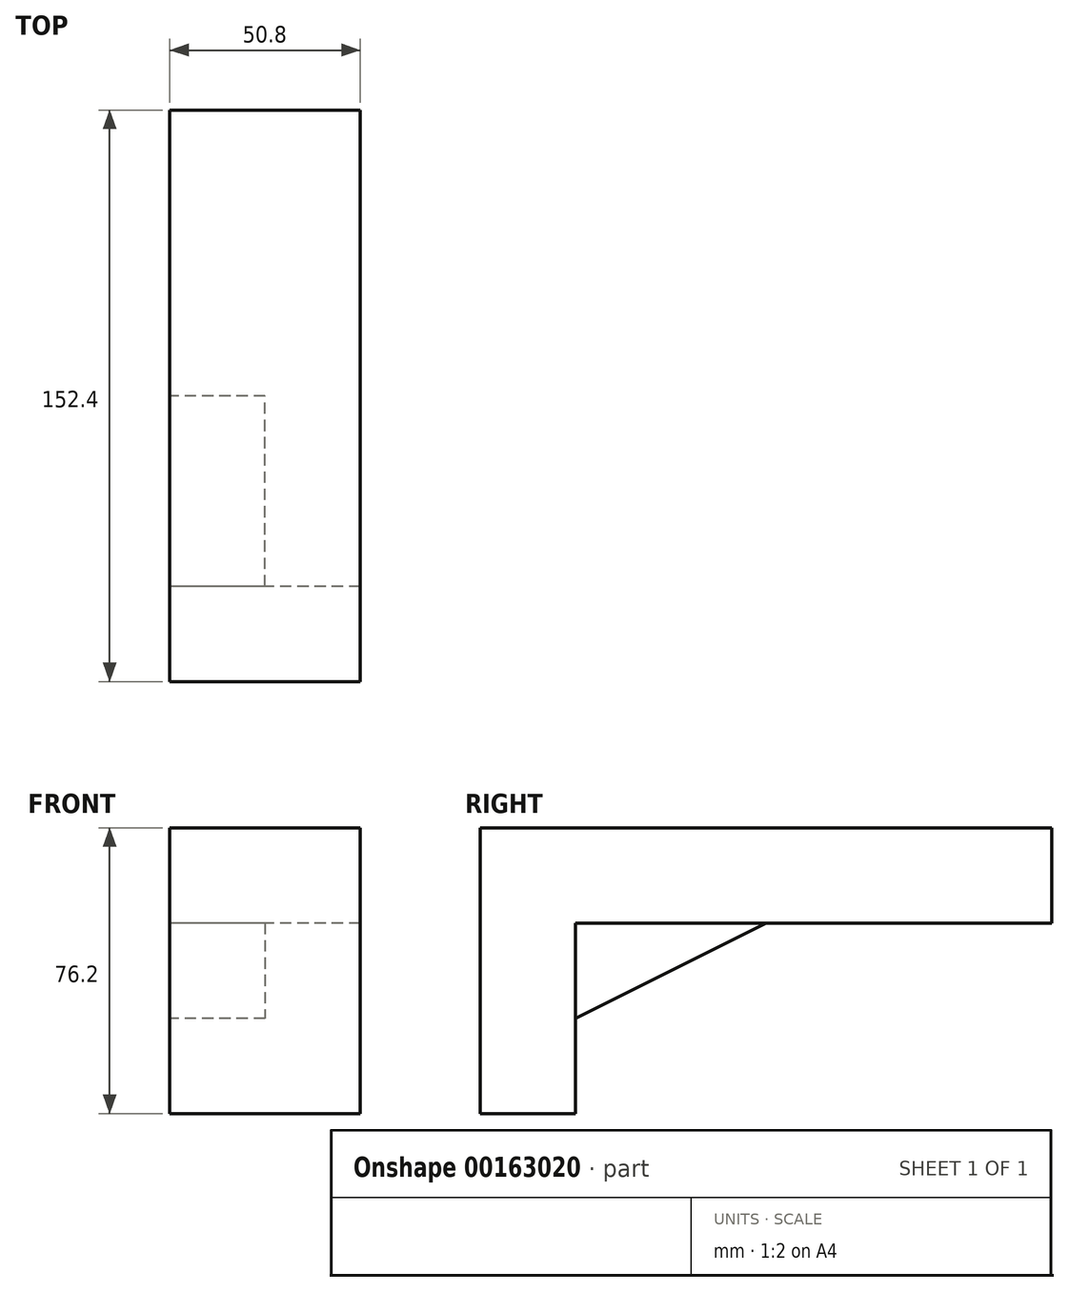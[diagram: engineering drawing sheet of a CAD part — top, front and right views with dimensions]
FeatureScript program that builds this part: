
annotation { "Feature Type Name" : "Feature", "Feature Type Description" : "" }
export const myFeature = defineFeature(function(context is Context, id is Id, definition is map)
    precondition{}
    {
        {
            var Q0;
            Q0=qCreatedBy(makeId("Right.planeOp"),FACE);
            var sketch = newSketch(context, id + "F0", { "sketchPlane" : qUnion([Q0])});
            skLineSegment(sketch, "E0", {"start": v(0, 0) * mm, "end": v(0, 76.2) * mm});
            skLineSegment(sketch, "E1", {"start": v(0, 0) * mm, "end": v(25.4, 0) * mm});
            skLineSegment(sketch, "E2", {"start": v(0, 76.2) * mm, "end": v(152.4, 76.2) * mm});
            skLineSegment(sketch, "E3", {"start": v(25.4, 0) * mm, "end": v(25.4, 50.8) * mm});
            skLineSegment(sketch, "E4", {"start": v(152.4, 76.2) * mm, "end": v(152.4, 50.8) * mm});
            skLineSegment(sketch, "E5", {"start": v(25.4, 50.8) * mm, "end": v(152.4, 50.8) * mm});
            skSolve(sketch);
        }
        {
            var Q0;
            Q0=makeQuery(id+"F0.imprint","IMPRINT",FACE,{"disambiguationData":[TD([[makeQuery(id+"F0.imprint","IMPRINT",EDGE,{"derivedFrom":sQuery(id+"F0.wireOp",EDGE,"E0")}),-1.0]])]});
            extrude(context, id + "F1", {"entities" : qUnion([Q0]), "depth" : 50.8 * mm});
        }
        {
            var Q0;
            Q0=qCreatedBy(makeId("Right.planeOp"),FACE);
            var sketch = newSketch(context, id + "F2", { "sketchPlane" : qUnion([Q0])});
            skLineSegment(sketch, "E6", {"start": v(25.4, 50.8) * mm, "end": v(76.2, 50.8) * mm});
            skLineSegment(sketch, "E7", {"start": v(25.4, 50.8) * mm, "end": v(25.4, 25.4) * mm});
            skLineSegment(sketch, "E8", {"start": v(25.4, 25.4) * mm, "end": v(76.2, 50.8) * mm});
            skSolve(sketch);
        }
        {
            var Q0;
            Q0=makeQuery(id+"F2.imprint","IMPRINT",FACE,{"disambiguationData":[TD([[makeQuery(id+"F2.imprint","IMPRINT",EDGE,{"derivedFrom":sQuery(id+"F2.wireOp",EDGE,"E6")}),-1.0]])]});
            extrude(context, id + "F3", {"entities" : qUnion([Q0]), "depth" : 25.4 * mm});
        }
    });
